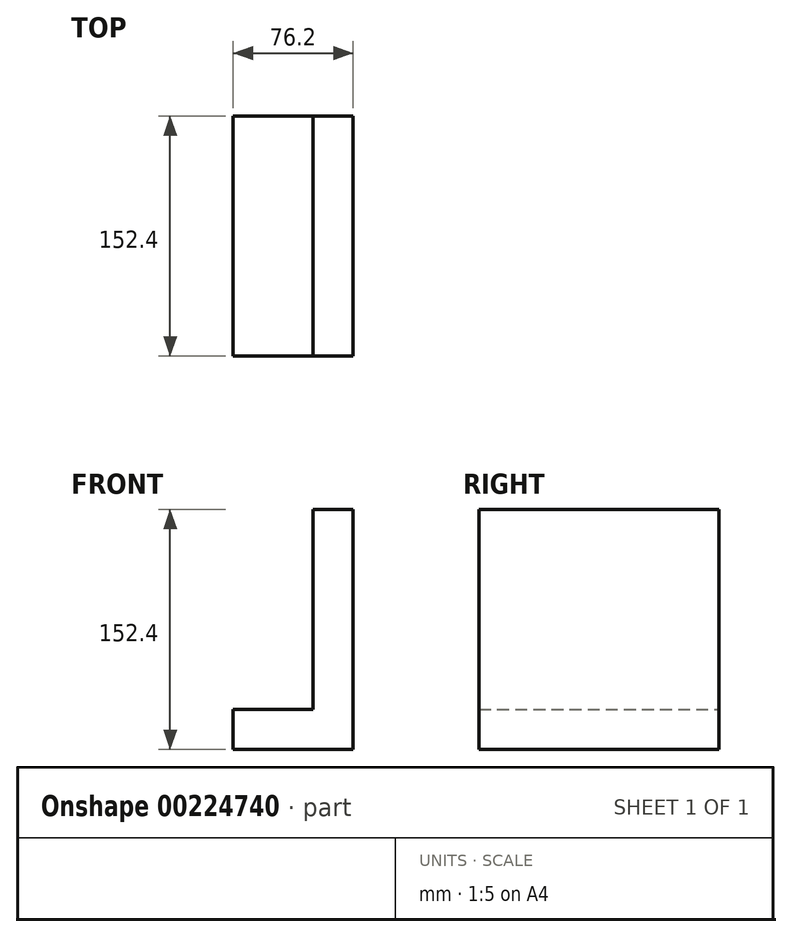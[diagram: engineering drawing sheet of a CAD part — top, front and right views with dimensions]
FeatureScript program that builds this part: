
annotation { "Feature Type Name" : "Feature", "Feature Type Description" : "" }
export const myFeature = defineFeature(function(context is Context, id is Id, definition is map)
    precondition{}
    {
        {
            var Q0;
            Q0=qCreatedBy(makeId("Front.planeOp"),FACE);
            var sketch = newSketch(context, id + "F0", { "sketchPlane" : qUnion([Q0])});
            skLineSegment(sketch, "E0", {"start": v(0, 0) * mm, "end": v(-76.2, 0) * mm});
            skLineSegment(sketch, "E1", {"start": v(0, 0) * mm, "end": v(0, 152.4) * mm});
            skLineSegment(sketch, "E2", {"start": v(0, 152.4) * mm, "end": v(-25.4, 152.4) * mm});
            skLineSegment(sketch, "E3", {"start": v(-25.4, 152.4) * mm, "end": v(-25.4, 25.4) * mm});
            skLineSegment(sketch, "E4", {"start": v(-25.4, 25.4) * mm, "end": v(-76.2, 25.4) * mm});
            skLineSegment(sketch, "E5", {"start": v(-76.2, 0) * mm, "end": v(-76.2, 25.4) * mm});
            skSolve(sketch);
        }
        {
            var Q0;
            Q0 = qSketchRegion(id + "F0", true);
            extrude(context, id + "F1", {"entities" : qUnion([Q0]), "endBound" : BoundingType.SYMMETRIC, "depth" : 152.4 * mm});
        }
    });
